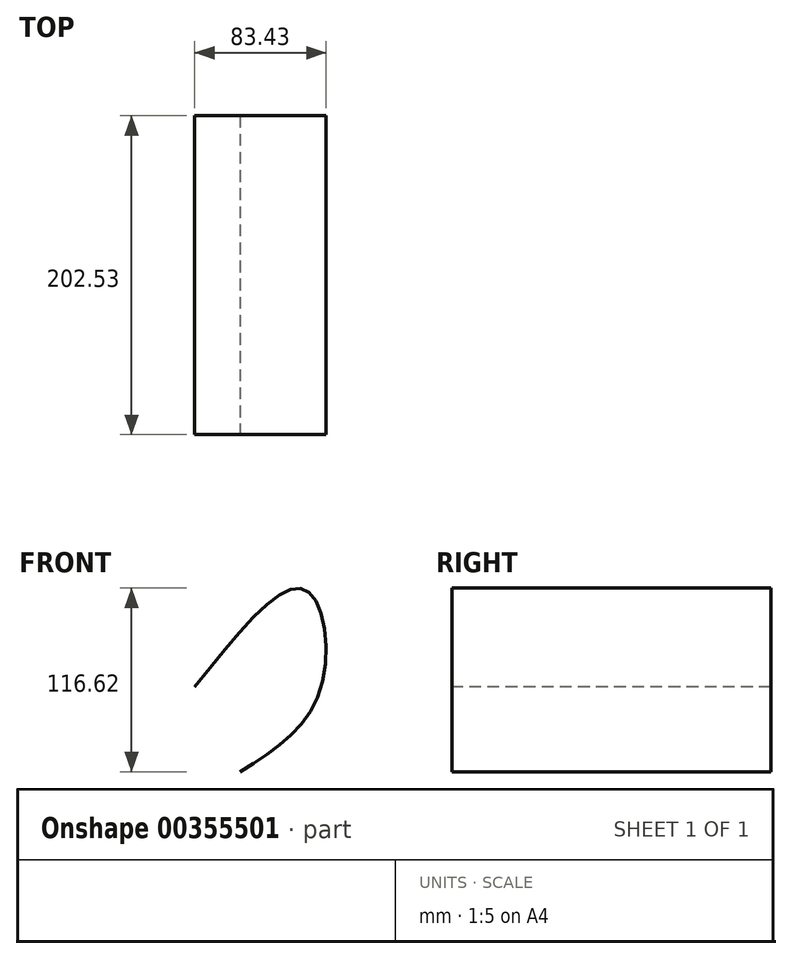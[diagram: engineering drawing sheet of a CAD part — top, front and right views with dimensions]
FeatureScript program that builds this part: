
annotation { "Feature Type Name" : "Feature", "Feature Type Description" : "" }
export const myFeature = defineFeature(function(context is Context, id is Id, definition is map)
    precondition{}
    {
        {
            var Q0;
            Q0=qCreatedBy(makeId("Front.planeOp"),FACE);
            var sketch = newSketch(context, id + "F0", { "sketchPlane" : qUnion([Q0])});
            skFitSpline(sketch, "E0", {"points": [v(-28.87, 17.6) * mm, v(41.14, 79.45) * mm, v(50.94, 15.82) * mm, v(0, -36.28) * mm], "startDerivative": vector(222.41, 279.85) * mm, "endDerivative": vector(-198.17, -123.74) * mm});
            skSolve(sketch);
        }
        {
            var Q0;
            Q0=sQuery(id+"F0.wireOp",EDGE,"E0");
            extrude(context, id + "F1", {"bodyType" : ToolBodyType.SURFACE, "surfaceEntities" : qUnion([Q0]), "depth" : 202.53 * mm});
        }
    });
